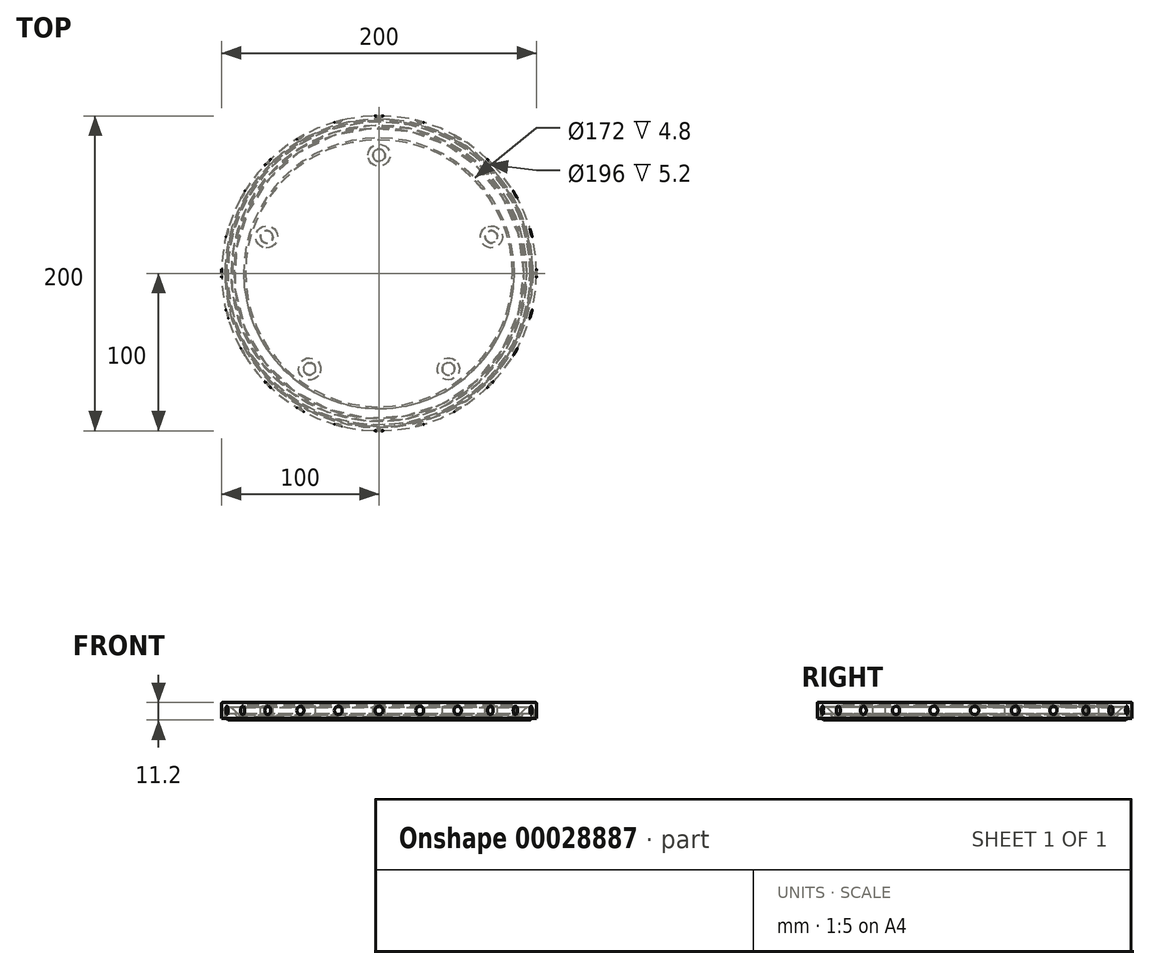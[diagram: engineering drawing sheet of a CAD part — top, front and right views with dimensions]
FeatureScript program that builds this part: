
annotation { "Feature Type Name" : "Feature", "Feature Type Description" : "" }
export const myFeature = defineFeature(function(context is Context, id is Id, definition is map)
    precondition{}
    {
        {
            var Q0;
            Q0=qCreatedBy(makeId("Top.planeOp"),FACE);
            var sketch = newSketch(context, id + "F0", { "sketchPlane" : qUnion([Q0])});
            skCircle(sketch, "E0", {"center": v(0, 0) * mm, "radius": 100 * mm, "construction": true});
            skSolve(sketch);
        }
        {
            var Q0;
            Q0=qCreatedBy(makeId("Right.planeOp"),FACE);
            var sketch = newSketch(context, id + "F1", { "sketchPlane" : qUnion([Q0])});
            skLineSegment(sketch, "E1", {"start": v(0, 0) * mm, "end": v(97, 0) * mm});
            skLineSegment(sketch, "E2", {"start": v(97, 0) * mm, "end": v(97, 4) * mm});
            skLineSegment(sketch, "E3", {"start": v(97, 4) * mm, "end": v(92, 4) * mm});
            skLineSegment(sketch, "E4", {"start": v(90, 2) * mm, "end": v(0, 2) * mm});
            skLineSegment(sketch, "E5", {"start": v(97, 0) * mm, "end": v(100, 0) * mm, "construction": true});
            skLineSegment(sketch, "E6", {"start": v(92, 4) * mm, "end": v(90, 2) * mm});
            skLineSegment(sketch, "E7", {"start": v(0, 2) * mm, "end": v(0, 0) * mm});
            skSolve(sketch);
        }
        {
            var Q0;
            Q0=qSketchRegion(id+"F1",true);
            var Q1;
            Q1=sQuery(id+"F1.wireOp",EDGE,"E7");
            revolve(context, id + "F2", {"entities" : qUnion([Q0]), "axis" : qUnion([Q1]), "revolveType" : RevolveType.FULL});
        }
        {
            var Q0;
            Q0=qCreatedBy(makeId("Right.planeOp"),FACE);
            var sketch = newSketch(context, id + "F3", { "sketchPlane" : qUnion([Q0])});
            skLineSegment(sketch, "E8", {"start": v(75, 2) * mm, "end": v(82, 2) * mm});
            skLineSegment(sketch, "E9", {"start": v(82, 2) * mm, "end": v(82, 2.2) * mm});
            skLineSegment(sketch, "E10", {"start": v(82, 2.2) * mm, "end": v(78.9, 2.2) * mm});
            skLineSegment(sketch, "E11", {"start": v(78.9, 2.2) * mm, "end": v(78.9, 8.7) * mm});
            skLineSegment(sketch, "E12", {"start": v(78.9, 8.7) * mm, "end": v(75, 8.7) * mm});
            skLineSegment(sketch, "E13", {"start": v(75, 8.7) * mm, "end": v(75, 2) * mm});
            skLineSegment(sketch, "E14", {"start": v(75, 2) * mm, "end": v(75, 0) * mm, "construction": true});
            skLineSegment(sketch, "E15", {"start": v(75, 0) * mm, "end": v(100, 0) * mm, "construction": true});
            skSolve(sketch);
        }
        {
            var Q0;
            Q0=qSketchRegion(id+"F3",true);
            var Q1;
            Q1=sQuery(id+"F3.wireOp",EDGE,"E13");
            revolve(context, id + "F4", {"operationType" : NewBodyOperationType.ADD, "entities" : qUnion([Q0]), "axis" : qUnion([Q1]), "revolveType" : RevolveType.FULL});
        }
        {
            var Q0;
            Q0=makeQuery(id+"F4.opRevolve","SWEPT_EDGE",EDGE,{"disambiguationData":[OSD([sQuery(id+"F3.wireOp",EDGE,"E11"),sQuery(id+"F3.wireOp",EDGE,"E12")])]});
            var Q1;
            Q1=makeQuery(id+"F4.opRevolve","SWEPT_EDGE",EDGE,{"disambiguationData":[OSD([sQuery(id+"F3.wireOp",EDGE,"E9"),sQuery(id+"F3.wireOp",EDGE,"E10")])]});
            fillet(context, id + "F5", {"entities" : qUnion([Q0, Q1]), "radius" : 1 * mm, "tangentPropagation" : true, "rho" : .7, "crossSection" : FilletCrossSection.CONIC, "allowEdgeOverflow" : false});
        }
        {
            var Q0;
            Q0=qCreatedBy(makeId("Right.planeOp"),FACE);
            var sketch = newSketch(context, id + "F6", { "sketchPlane" : qUnion([Q0])});
            skLineSegment(sketch, "E16", {"start": v(0, 0) * mm, "end": v(0, 45.85) * mm});
            skSolve(sketch);
        }
        {
            var Q0;
            Q0=makeQuery(id+"F2.opRevolve","SWEPT_BODY",BODY,{"disambiguationData":[OSD([sQuery(id+"F1.wireOp",EDGE,"E1"),sQuery(id+"F1.wireOp",EDGE,"E2"),sQuery(id+"F1.wireOp",EDGE,"E3"),sQuery(id+"F1.wireOp",EDGE,"E4"),sQuery(id+"F1.wireOp",EDGE,"E6"),sQuery(id+"F1.wireOp",EDGE,"E7")])]});
            var Q1;
            Q1=makeQuery(id+"F4.opRevolve","SWEPT_FACE",FACE,{"disambiguationData":[OSD([sQuery(id+"F3.wireOp",EDGE,"E10")])]});
            var Q2;
            Q2=makeQuery(id+"F4.opRevolve","SWEPT_FACE",FACE,{"disambiguationData":[OSD([sQuery(id+"F3.wireOp",EDGE,"E12")])]});
            var Q3;
            Q3=makeQuery(id+"F5.opFillet","BLEND_FACE",FACE,{"disambiguationData":[OSD([sQuery(id+"F3.wireOp",EDGE,"E11"),sQuery(id+"F3.wireOp",EDGE,"E12")])]});
            var Q4;
            Q4=makeQuery(id+"F4.opRevolve","SWEPT_FACE",FACE,{"disambiguationData":[OSD([sQuery(id+"F3.wireOp",EDGE,"E11")])]});
            var Q5;
            Q5=makeQuery(id+"F5.opFillet","BLEND_FACE",FACE,{"disambiguationData":[OSD([sQuery(id+"F3.wireOp",EDGE,"E9"),sQuery(id+"F3.wireOp",EDGE,"E10")])]});
            var Q6;
            Q6=sQuery(id+"F6.wireOp",EDGE,"E16");
            circularPattern(context, id + "F7", {"operationType" : NewBodyOperationType.ADD, "entities" : qUnion([Q0]), "axis" : qUnion([Q6]), "angle" : 360 * degree, "instanceCount" : 5, "equalSpace" : true});
        }
        {
            var Q0;
            Q0=makeQuery(id+"F2.opRevolve","SWEPT_FACE",FACE,{"disambiguationData":[OSD([sQuery(id+"F1.wireOp",EDGE,"E1")])]});
            var sketch = newSketch(context, id + "F8", { "sketchPlane" : qUnion([Q0])});
            skCircle(sketch, "E17", {"center": v(0, 0) * mm, "radius": 93 * mm});
            skSolve(sketch);
        }
        {
            var Q0;
            Q0=qCreatedBy(makeId("Right.planeOp"),FACE);
            var sketch = newSketch(context, id + "F9", { "sketchPlane" : qUnion([Q0])});
            skCircle(sketch, "E18", {"center": v(-93, 0.4) * mm, "radius": 0.9 * mm});
            skLineSegment(sketch, "E19", {"start": v(-93, 0.4) * mm, "end": v(-93, 0) * mm, "construction": true});
            skLineSegment(sketch, "E20", {"start": v(-93, 0) * mm, "end": v(-93, -0.5) * mm, "construction": true});
            skSolve(sketch);
        }
        {
            var Q0;
            Q0=qSketchRegion(id+"F9",true);
            var Q1;
            Q1=sQuery(id+"F8.wireOp",EDGE,"E17");
            sweep(context, id + "F10", {"operationType" : NewBodyOperationType.REMOVE, "profiles" : qUnion([Q0]), "path" : qUnion([Q1])});
        }
        {
            var Q0;
            Q0=qCreatedBy(makeId("Right.planeOp"),FACE);
            var sketch = newSketch(context, id + "F11", { "sketchPlane" : qUnion([Q0])});
            skLineSegment(sketch, "E21", {"start": v(0, 9.2) * mm, "end": v(0, 11.2) * mm});
            skLineSegment(sketch, "E22", {"start": v(0, 11.2) * mm, "end": v(100, 11.2) * mm});
            skLineSegment(sketch, "E23", {"start": v(100, 11.2) * mm, "end": v(100, 1) * mm});
            skLineSegment(sketch, "E24", {"start": v(100, 1) * mm, "end": v(98, 1) * mm});
            skLineSegment(sketch, "E25", {"start": v(98, 1) * mm, "end": v(98, 8.2) * mm});
            skLineSegment(sketch, "E26", {"start": v(98, 8.2) * mm, "end": v(94, 8.2) * mm});
            skLineSegment(sketch, "E27", {"start": v(94, 8.2) * mm, "end": v(89, 3.2) * mm});
            skLineSegment(sketch, "E28", {"start": v(89, 3.2) * mm, "end": v(86, 3.2) * mm});
            skLineSegment(sketch, "E29", {"start": v(86, 3.2) * mm, "end": v(86, 9.2) * mm});
            skLineSegment(sketch, "E30", {"start": v(86, 9.2) * mm, "end": v(0, 9.2) * mm});
            skLineSegment(sketch, "E31", {"start": v(100, 1) * mm, "end": v(100, 0) * mm, "construction": true});
            skLineSegment(sketch, "E32", {"start": v(86, 3.2) * mm, "end": v(86, 0) * mm, "construction": true});
            skLineSegment(sketch, "E33", {"start": v(86, 0) * mm, "end": v(100, 0) * mm, "construction": true});
            skSolve(sketch);
        }
        {
            var Q0;
            Q0=qSketchRegion(id+"F11",true);
            var Q1;
            Q1=sQuery(id+"F11.wireOp",EDGE,"E21");
            revolve(context, id + "F12", {"entities" : qUnion([Q0]), "axis" : qUnion([Q1]), "revolveType" : RevolveType.FULL});
        }
        {
            var Q0;
            Q0=makeQuery(id+"F2.opRevolve","SWEPT_EDGE",EDGE,{"disambiguationData":[OSD([sQuery(id+"F1.wireOp",EDGE,"E3"),sQuery(id+"F1.wireOp",EDGE,"E6")])]});
            var Q1;
            Q1=makeQuery(id+"F2.opRevolve","SWEPT_EDGE",EDGE,{"disambiguationData":[OSD([sQuery(id+"F1.wireOp",EDGE,"E4"),sQuery(id+"F1.wireOp",EDGE,"E6")])]});
            var Q2;
            Q2=makeQuery(id+"F2.opRevolve","SWEPT_EDGE",EDGE,{"disambiguationData":[OSD([sQuery(id+"F1.wireOp",EDGE,"E2"),sQuery(id+"F1.wireOp",EDGE,"E3")])]});
            fillet(context, id + "F13", {"entities" : qUnion([Q0, Q1, Q2]), "radius" : 2 * mm, "tangentPropagation" : true, "rho" : .7, "crossSection" : FilletCrossSection.CONIC, "allowEdgeOverflow" : false});
        }
        {
            var Q0;
            Q0=makeQuery(id+"F12.opRevolve","SWEPT_EDGE",EDGE,{"disambiguationData":[OSD([sQuery(id+"F11.wireOp",EDGE,"E25"),sQuery(id+"F11.wireOp",EDGE,"E26")])]});
            var Q1;
            Q1=makeQuery(id+"F12.opRevolve","SWEPT_EDGE",EDGE,{"disambiguationData":[OSD([sQuery(id+"F11.wireOp",EDGE,"E26"),sQuery(id+"F11.wireOp",EDGE,"E27")])]});
            var Q2;
            Q2=makeQuery(id+"F12.opRevolve","SWEPT_EDGE",EDGE,{"disambiguationData":[OSD([sQuery(id+"F11.wireOp",EDGE,"E27"),sQuery(id+"F11.wireOp",EDGE,"E28")])]});
            fillet(context, id + "F14", {"entities" : qUnion([Q0, Q1, Q2]), "radius" : 2 * mm, "tangentPropagation" : true, "rho" : .7, "crossSection" : FilletCrossSection.CONIC, "allowEdgeOverflow" : false});
        }
        {
            var Q0;
            Q0=makeQuery(id+"F12.opRevolve","SWEPT_EDGE",EDGE,{"disambiguationData":[OSD([sQuery(id+"F11.wireOp",EDGE,"E29"),sQuery(id+"F11.wireOp",EDGE,"E30")])]});
            chamfer(context, id + "F15", {"entities" : qUnion([Q0]), "width" : 1.2 * mm, "tangentPropagation" : true});
        }
        {
            var Q0;
            Q0=makeQuery(id+"F12.opRevolve","SWEPT_EDGE",EDGE,{"disambiguationData":[OSD([sQuery(id+"F11.wireOp",EDGE,"E22"),sQuery(id+"F11.wireOp",EDGE,"E23")])]});
            fillet(context, id + "F16", {"entities" : qUnion([Q0]), "radius" : 1 * mm, "tangentPropagation" : true, "rho" : .6, "crossSection" : FilletCrossSection.CONIC, "allowEdgeOverflow" : false});
        }
        {
            var Q0;
            Q0=makeQuery(id+"F10.boolean.opBoolean","INTERSECT",EDGE,{"disambiguationData":[OD(1.0)],"derivedFrom":[makeQuery(id+"F2.opRevolve","SWEPT_FACE",FACE,{"disambiguationData":[OSD([sQuery(id+"F1.wireOp",EDGE,"E1")])]}),makeQuery(id+"F10.opSweep","SWEPT_FACE",FACE,{"disambiguationData":[OSD([sQuery(id+"F8.wireOp",EDGE,"E17"),sQuery(id+"F9.wireOp",EDGE,"E18")])]})]});
            var Q1;
            Q1=makeQuery(id+"F10.boolean.opBoolean","INTERSECT",EDGE,{"disambiguationData":[OD(0.0)],"derivedFrom":[makeQuery(id+"F2.opRevolve","SWEPT_FACE",FACE,{"disambiguationData":[OSD([sQuery(id+"F1.wireOp",EDGE,"E1")])]}),makeQuery(id+"F10.opSweep","SWEPT_FACE",FACE,{"disambiguationData":[OSD([sQuery(id+"F8.wireOp",EDGE,"E17"),sQuery(id+"F9.wireOp",EDGE,"E18")])]})]});
            chamfer(context, id + "F17", {"entities" : qUnion([Q0, Q1]), "chamferType" : ChamferType.OFFSET_ANGLE, "width" : .1 * mm, "oppositeDirection" : true, "angle" : 90 * degree, "tangentPropagation" : true});
        }
        {
            var Q0;
            Q0=makeQuery(id+"F2.opRevolve","SWEPT_EDGE",EDGE,{"disambiguationData":[OSD([sQuery(id+"F1.wireOp",EDGE,"E1"),sQuery(id+"F1.wireOp",EDGE,"E2")])]});
            chamfer(context, id + "F18", {"entities" : qUnion([Q0]), "width" : 1 * mm, "tangentPropagation" : true});
        }
        {
            var Q0;
            Q0=qCreatedBy(makeId("Right.planeOp"),FACE);
            var sketch = newSketch(context, id + "F19", { "sketchPlane" : qUnion([Q0])});
            skLineSegment(sketch, "E34", {"start": v(104.2, 11.1) * mm, "end": v(104.2, 1.1) * mm});
            skLineSegment(sketch, "E35", {"start": v(104.2, 1.1) * mm, "end": v(104.2, 0) * mm, "construction": true});
            skLineSegment(sketch, "E36", {"start": v(104.2, 0) * mm, "end": v(100, 0) * mm, "construction": true});
            skLineSegment(sketch, "E37", {"start": v(104.2, 6.1) * mm, "end": v(99, 6.1) * mm, "construction": true});
            skLineSegment(sketch, "E38", {"start": v(99, 11.2) * mm, "end": v(99, 1) * mm, "construction": true});
            skArc(sketch, "E39", {"start": v(104.2, 11.1) * mm, "mid": v(99.2, 6.1) * mm, "end": v(104.2, 1.1) * mm});
            skSolve(sketch);
        }
        {
            var Q0;
            Q0=makeQuery(id+"F19.imprint","IMPRINT",FACE,{"disambiguationData":[TD([[makeQuery(id+"F19.imprint","IMPRINT",EDGE,{"derivedFrom":sQuery(id+"F19.wireOp",EDGE,"E34")}),-1.0]])]});
            var Q1;
            Q1=sQuery(id+"F19.wireOp",EDGE,"E34");
            revolve(context, id + "F20", {"operationType" : NewBodyOperationType.REMOVE, "entities" : qUnion([Q0]), "axis" : qUnion([Q1]), "revolveType" : RevolveType.FULL, "oppositeDirection" : true});
        }
        {
            var Q0;
            Q0=makeQuery(id+"F12.opRevolve","SWEPT_BODY",BODY,{"disambiguationData":[OSD([sQuery(id+"F11.wireOp",EDGE,"E21"),sQuery(id+"F11.wireOp",EDGE,"E22"),sQuery(id+"F11.wireOp",EDGE,"E23"),sQuery(id+"F11.wireOp",EDGE,"E24"),sQuery(id+"F11.wireOp",EDGE,"E25"),sQuery(id+"F11.wireOp",EDGE,"E26"),sQuery(id+"F11.wireOp",EDGE,"E27"),sQuery(id+"F11.wireOp",EDGE,"E28"),sQuery(id+"F11.wireOp",EDGE,"E29"),sQuery(id+"F11.wireOp",EDGE,"E30")])]});
            var Q1;
            Q1=makeQuery(id+"F20.boolean.opBoolean","COPY",FACE,{"derivedFrom":makeQuery(id+"F20.opRevolve","SWEPT_FACE",FACE,{"disambiguationData":[OSD([sQuery(id+"F19.wireOp",EDGE,"E39")])]})});
            var Q2;
            Q2=sQuery(id+"F6.wireOp",EDGE,"E16");
            circularPattern(context, id + "F21", {"faces" : qUnion([Q1]), "axis" : qUnion([Q2]), "angle" : 360 * degree, "instanceCount" : 24, "equalSpace" : true, "patternType" : PatternType.FACE});
        }
    });
